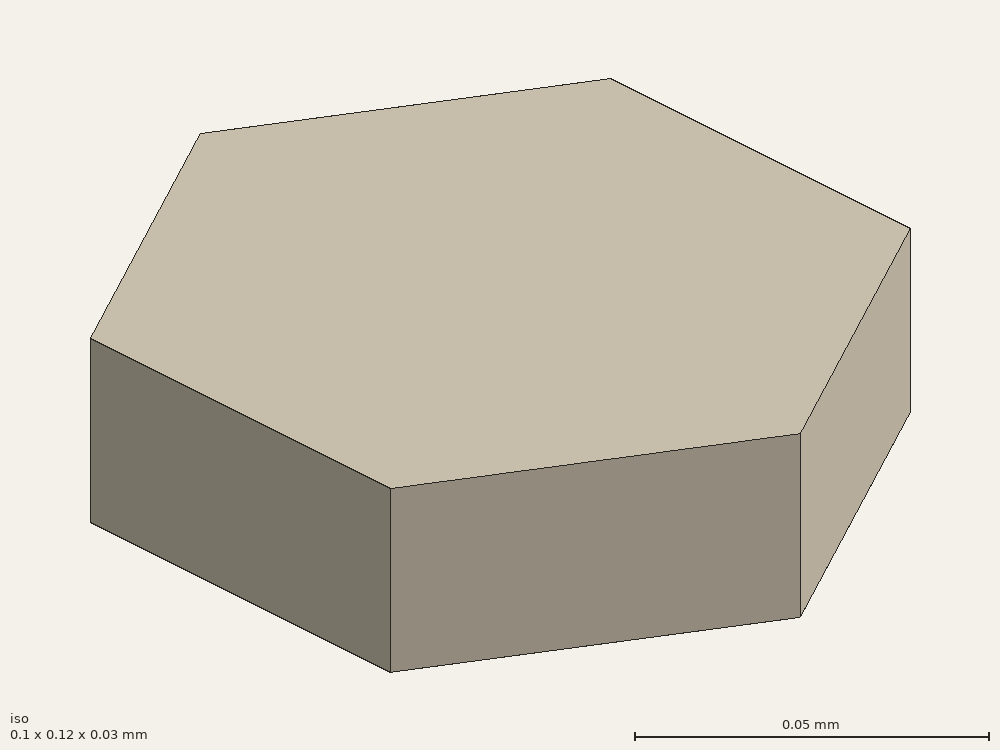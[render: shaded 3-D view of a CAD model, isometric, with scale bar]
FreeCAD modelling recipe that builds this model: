
FCSTD DOCUMENT  (FreeCAD 0.15R4671 (Git))
Label: hexagorangle0
License: All rights reserved
LicenseURL: http://en.wikipedia.org/wiki/All_rights_reserved
objects: Sketcher::SketchObject×1, PartDesign::Pad×1
note: 3 computed .brp shape members not serialized (recipe doc carries the construction recipe); baked Part::Feature solids carry a one-line shape summary decoded from their .brp

FEATURE [Sketcher::SketchObject] Sketch001
  sketch-geometry (6):
    g0: LineSegment StartX=0.0519615 StartY=0.03 StartZ=0 EndX=0.0519615 EndY=-0.03 EndZ=0
    g1: LineSegment StartX=0.0519615 StartY=-0.03 StartZ=0 EndX=0 EndY=-0.06 EndZ=0
    g2: LineSegment StartX=0 StartY=-0.06 StartZ=0 EndX=-0.0519615 EndY=-0.03 EndZ=0
    g3: LineSegment StartX=-0.0519615 StartY=-0.03 StartZ=0 EndX=-0.0519615 EndY=0.03 EndZ=0
    g4: LineSegment StartX=-0.0519615 StartY=0.03 StartZ=0 EndX=0 EndY=0.06 EndZ=0
    g5: LineSegment StartX=0 StartY=0.06 StartZ=0 EndX=0.0519615 EndY=0.03 EndZ=0
  constraints (18):
    c: Coincident(g1,g0)
    c: Coincident(g2,g1)
    c: Coincident(g4,g3)
    c: Coincident(g5,g4)
    c: Coincident(g5,g0)
    c: Coincident(g3,g2)
    c: Parallel(g3,g0)
    c: Parallel(g4,g1)
    c: Equal(g3,g2)
    c: Equal(g2,g1)
    c: Equal(g1,g0)
    c: Equal(g0,g5)
    c: Equal(g5,g4)
    c: Angle(g4,g5) = 2.0944
    c: Angle(g5,g0) = 2.0944
    c: Symmetric(g1,g4,g-1)
    c: Distance(g3) = 0.06
    c: Parallel(g3,g-2)
FEATURE [PartDesign::Pad] Pad
  Length = 0.03
  Length2 = 100
  Sketch = -> Sketch001
  Type = 0
